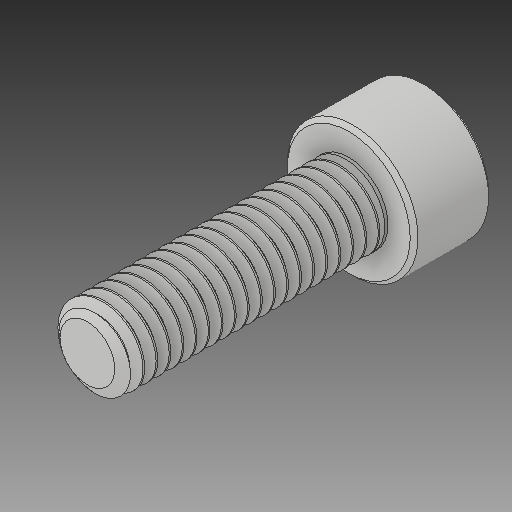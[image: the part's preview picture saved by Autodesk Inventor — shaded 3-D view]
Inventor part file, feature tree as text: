
AUTODESK INVENTOR PART (.ipt)
format: ipt  version: 2018 (Build 220112000, 112)  size: 890,368 bytes
history: native  units: in
note: dims shown in document units (in); Inventor stores cm internally (conversion verified against a paired STEP export)
features: revolve x1
ambient origin geometry x8: Origin, YZ Plane, XZ Plane, XY Plane, X Axis, Y Axis, Z Axis, Center Point
bodies: Solid1 (feature_tree)
feature tree (1):
  revolve  "Revolve1"  [1 undecoded]
note: 1 required parameter value undecoded (feature->parameter linkage not recoverable at this tier; creation-order binding heuristic only, values carry confidence <= 0.55)
